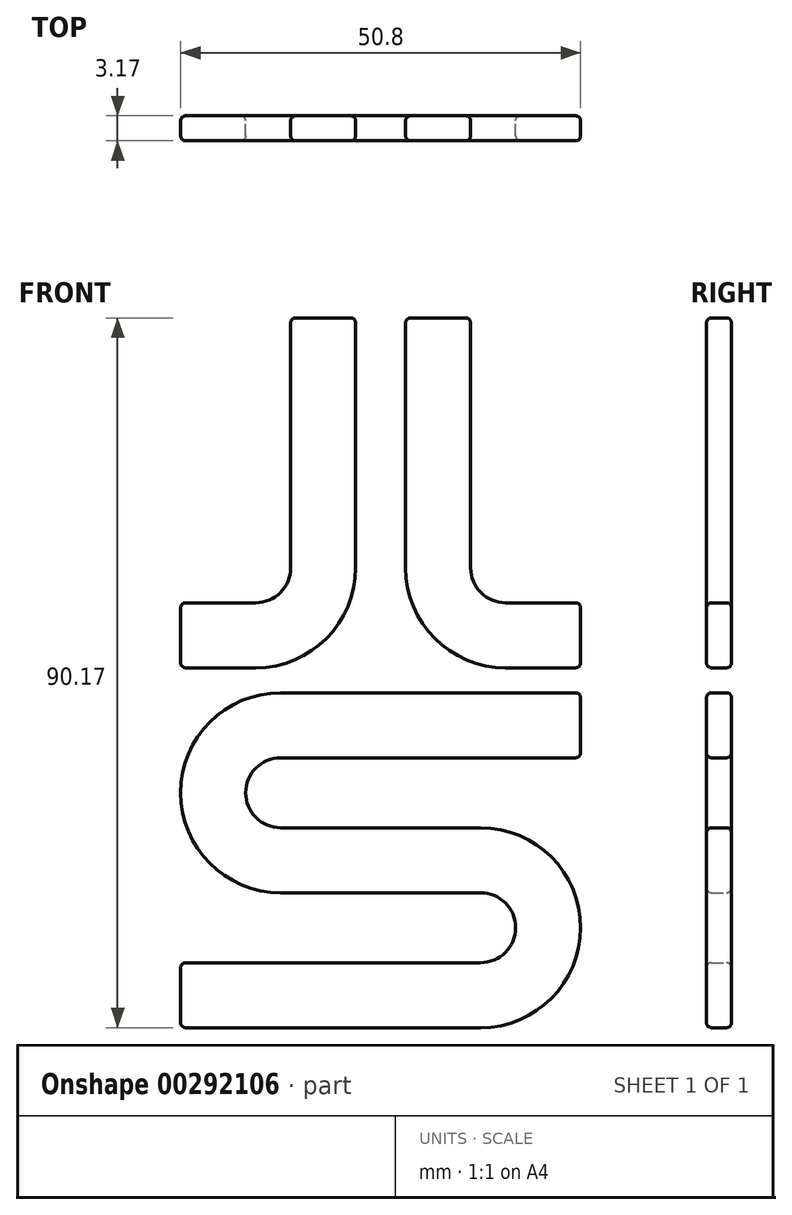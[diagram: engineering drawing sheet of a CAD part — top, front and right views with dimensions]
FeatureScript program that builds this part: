
annotation { "Feature Type Name" : "Feature", "Feature Type Description" : "" }
export const myFeature = defineFeature(function(context is Context, id is Id, definition is map)
    precondition{}
    {
        {
            var Q0;
            Q0=qCreatedBy(makeId("Front.planeOp"),FACE);
            var sketch = newSketch(context, id + "F0", { "sketchPlane" : qUnion([Q0])});
            skLineSegment(sketch, "E0.bottom", {"start": v(-11.43, 44.45) * mm, "end": v(-3.17, 44.45) * mm});
            skLineSegment(sketch, "E0.left", {"start": v(-11.43, 44.45) * mm, "end": v(-11.43, 12.7) * mm});
            skLineSegment(sketch, "E0.right", {"start": v(-3.17, 44.45) * mm, "end": v(-3.17, 12.7) * mm});
            skLineSegment(sketch, "E1.bottom", {"start": v(-15.87, 8.26) * mm, "end": v(-25.4, 8.26) * mm});
            skLineSegment(sketch, "E1.top", {"start": v(-15.87, 0) * mm, "end": v(-25.4, 0) * mm});
            skLineSegment(sketch, "E1.right", {"start": v(-25.4, 8.26) * mm, "end": v(-25.4, 0) * mm});
            skArc(sketch, "E2", {"start": v(-11.43, 12.7) * mm, "mid": v(-12.73, 9.56) * mm, "end": v(-15.87, 8.26) * mm});
            skArc(sketch, "E3", {"start": v(-3.17, 12.7) * mm, "mid": v(-6.9, 3.72) * mm, "end": v(-15.87, 0) * mm});
            skLineSegment(sketch, "E4", {"start": v(0, 0) * mm, "end": v(0, 65.18) * mm, "construction": true});
            skLineSegment(sketch, "E5.MirrorCS", {"start": v(11.43, 44.45) * mm, "end": v(3.17, 44.45) * mm});
            skLineSegment(sketch, "E6.MirrorCS", {"start": v(11.43, 44.45) * mm, "end": v(11.43, 12.7) * mm});
            skLineSegment(sketch, "E7.MirrorCS", {"start": v(3.17, 44.45) * mm, "end": v(3.17, 12.7) * mm});
            skArc(sketch, "E8.MirrorCS", {"start": v(3.17, 12.7) * mm, "mid": v(6.9, 3.72) * mm, "end": v(15.87, 0) * mm});
            skArc(sketch, "E9.MirrorCS", {"start": v(11.43, 12.7) * mm, "mid": v(12.73, 9.56) * mm, "end": v(15.87, 8.26) * mm});
            skLineSegment(sketch, "E10.MirrorCS", {"start": v(15.87, 8.26) * mm, "end": v(25.4, 8.26) * mm});
            skLineSegment(sketch, "E11.MirrorCS", {"start": v(15.87, 0) * mm, "end": v(25.4, 0) * mm});
            skLineSegment(sketch, "E12.MirrorCS", {"start": v(25.4, 8.26) * mm, "end": v(25.4, 0) * mm});
            skLineSegment(sketch, "E13.bottom", {"start": v(25.4, -3.17) * mm, "end": v(-12.7, -3.17) * mm});
            skLineSegment(sketch, "E13.top", {"start": v(25.4, -11.43) * mm, "end": v(-12.7, -11.43) * mm});
            skLineSegment(sketch, "E13.left", {"start": v(25.4, -3.17) * mm, "end": v(25.4, -11.43) * mm});
            skLineSegment(sketch, "E14.bottom", {"start": v(12.7, -20.32) * mm, "end": v(-12.7, -20.32) * mm});
            skLineSegment(sketch, "E14.top", {"start": v(12.7, -28.57) * mm, "end": v(-12.7, -28.57) * mm});
            skLineSegment(sketch, "E15.bottom", {"start": v(12.7, -37.46) * mm, "end": v(-25.4, -37.46) * mm});
            skLineSegment(sketch, "E15.top", {"start": v(12.7, -45.72) * mm, "end": v(-25.4, -45.72) * mm});
            skLineSegment(sketch, "E15.right", {"start": v(-25.4, -37.46) * mm, "end": v(-25.4, -45.72) * mm});
            skArc(sketch, "E16", {"start": v(-12.7, -11.43) * mm, "mid": v(-17.15, -15.87) * mm, "end": v(-12.7, -20.32) * mm});
            skArc(sketch, "E17", {"start": v(-12.7, -3.17) * mm, "mid": v(-25.4, -15.87) * mm, "end": v(-12.7, -28.57) * mm});
            skArc(sketch, "E18", {"start": v(12.7, -20.32) * mm, "mid": v(25.4, -33.02) * mm, "end": v(12.7, -45.72) * mm});
            skArc(sketch, "E19", {"start": v(12.7, -28.57) * mm, "mid": v(17.15, -33.02) * mm, "end": v(12.7, -37.46) * mm});
            skLineSegment(sketch, "E20", {"start": v(25.4, -11.43) * mm, "end": v(25.4, -33.02) * mm, "construction": true});
            skLineSegment(sketch, "E21", {"start": v(-25.4, -37.46) * mm, "end": v(-25.4, -15.87) * mm, "construction": true});
            skLineSegment(sketch, "E22", {"start": v(25.4, 0) * mm, "end": v(25.4, -3.17) * mm, "construction": true});
            skLineSegment(sketch, "E23", {"start": v(-12.7, -3.17) * mm, "end": v(-12.7, -11.43) * mm, "construction": true});
            skLineSegment(sketch, "E24", {"start": v(12.7, -20.32) * mm, "end": v(12.7, -28.57) * mm, "construction": true});
            skLineSegment(sketch, "E25", {"start": v(12.7, -37.46) * mm, "end": v(12.7, -45.72) * mm, "construction": true});
            skLineSegment(sketch, "E26", {"start": v(-3.17, 44.45) * mm, "end": v(0, 44.45) * mm, "construction": true});
            skSolve(sketch);
        }
        {
            var Q0;
            Q0 = qSketchRegion(id + "F0", true);
            extrude(context, id + "F1", {"entities" : qUnion([Q0]), "depth" : 3.17 * mm});
        }
        {
            var Q0;
            Q0=makeQuery(id+"F1.opExtrude","CAP_FACE",FACE,{"disambiguationData":[OSD([sQuery(id+"F0.wireOp",EDGE,"E13.bottom"),sQuery(id+"F0.wireOp",EDGE,"E13.top"),sQuery(id+"F0.wireOp",EDGE,"E13.left"),sQuery(id+"F0.wireOp",EDGE,"E14.bottom"),sQuery(id+"F0.wireOp",EDGE,"E14.top"),sQuery(id+"F0.wireOp",EDGE,"E15.bottom"),sQuery(id+"F0.wireOp",EDGE,"E15.top"),sQuery(id+"F0.wireOp",EDGE,"E15.right"),sQuery(id+"F0.wireOp",EDGE,"E16"),sQuery(id+"F0.wireOp",EDGE,"E17"),sQuery(id+"F0.wireOp",EDGE,"E18"),sQuery(id+"F0.wireOp",EDGE,"E19")])],"isStart":false});
            var sketch = newSketch(context, id + "F2", { "sketchPlane" : qUnion([Q0])});
            skSolve(sketch);
        }
        {
            var Q0;
            Q0=makeQuery(id+"F1.opExtrude","CAP_FACE",FACE,{"disambiguationData":[OSD([sQuery(id+"F0.wireOp",EDGE,"E5.MirrorCS"),sQuery(id+"F0.wireOp",EDGE,"E6.MirrorCS"),sQuery(id+"F0.wireOp",EDGE,"E7.MirrorCS"),sQuery(id+"F0.wireOp",EDGE,"E8.MirrorCS"),sQuery(id+"F0.wireOp",EDGE,"E9.MirrorCS"),sQuery(id+"F0.wireOp",EDGE,"E10.MirrorCS"),sQuery(id+"F0.wireOp",EDGE,"E11.MirrorCS"),sQuery(id+"F0.wireOp",EDGE,"E12.MirrorCS")])],"isStart":false});
            var Q1;
            Q1=makeQuery(id+"F1.opExtrude","CAP_FACE",FACE,{"disambiguationData":[OSD([sQuery(id+"F0.wireOp",EDGE,"E0.bottom"),sQuery(id+"F0.wireOp",EDGE,"E0.left"),sQuery(id+"F0.wireOp",EDGE,"E0.right"),sQuery(id+"F0.wireOp",EDGE,"E1.bottom"),sQuery(id+"F0.wireOp",EDGE,"E1.top"),sQuery(id+"F0.wireOp",EDGE,"E1.right"),sQuery(id+"F0.wireOp",EDGE,"E2"),sQuery(id+"F0.wireOp",EDGE,"E3")])],"isStart":false});
            var Q2;
            Q2=makeQuery(id+"F1.opExtrude","CAP_FACE",FACE,{"disambiguationData":[OSD([sQuery(id+"F0.wireOp",EDGE,"E13.bottom"),sQuery(id+"F0.wireOp",EDGE,"E13.top"),sQuery(id+"F0.wireOp",EDGE,"E13.left"),sQuery(id+"F0.wireOp",EDGE,"E14.bottom"),sQuery(id+"F0.wireOp",EDGE,"E14.top"),sQuery(id+"F0.wireOp",EDGE,"E15.bottom"),sQuery(id+"F0.wireOp",EDGE,"E15.top"),sQuery(id+"F0.wireOp",EDGE,"E15.right"),sQuery(id+"F0.wireOp",EDGE,"E16"),sQuery(id+"F0.wireOp",EDGE,"E17"),sQuery(id+"F0.wireOp",EDGE,"E18"),sQuery(id+"F0.wireOp",EDGE,"E19")])],"isStart":false});
            var Q3;
            Q3=makeQuery(id+"F1.opExtrude","SWEPT_FACE",FACE,{"disambiguationData":[OSD([sQuery(id+"F0.wireOp",EDGE,"E12.MirrorCS")])]});
            var Q4;
            Q4=makeQuery(id+"F1.opExtrude","SWEPT_FACE",FACE,{"disambiguationData":[OSD([sQuery(id+"F0.wireOp",EDGE,"E13.left")])]});
            var Q5;
            Q5=makeQuery(id+"F1.opExtrude","SWEPT_FACE",FACE,{"disambiguationData":[OSD([sQuery(id+"F0.wireOp",EDGE,"E18")])]});
            var Q6;
            Q6=makeQuery(id+"F1.opExtrude","SWEPT_FACE",FACE,{"disambiguationData":[OSD([sQuery(id+"F0.wireOp",EDGE,"E15.bottom")])]});
            var Q7;
            Q7=makeQuery(id+"F1.opExtrude","SWEPT_FACE",FACE,{"disambiguationData":[OSD([sQuery(id+"F0.wireOp",EDGE,"E1.right")])]});
            var Q8;
            Q8=makeQuery(id+"F1.opExtrude","SWEPT_FACE",FACE,{"disambiguationData":[OSD([sQuery(id+"F0.wireOp",EDGE,"E5.MirrorCS")])]});
            var Q9;
            Q9=makeQuery(id+"F1.opExtrude","SWEPT_FACE",FACE,{"disambiguationData":[OSD([sQuery(id+"F0.wireOp",EDGE,"E0.bottom")])]});
            var Q10;
            Q10=makeQuery(id+"F1.opExtrude","CAP_FACE",FACE,{"disambiguationData":[OSD([sQuery(id+"F0.wireOp",EDGE,"E0.bottom"),sQuery(id+"F0.wireOp",EDGE,"E0.left"),sQuery(id+"F0.wireOp",EDGE,"E0.right"),sQuery(id+"F0.wireOp",EDGE,"E1.bottom"),sQuery(id+"F0.wireOp",EDGE,"E1.top"),sQuery(id+"F0.wireOp",EDGE,"E1.right"),sQuery(id+"F0.wireOp",EDGE,"E2"),sQuery(id+"F0.wireOp",EDGE,"E3")])],"isStart":true});
            var Q11;
            Q11=makeQuery(id+"F1.opExtrude","CAP_FACE",FACE,{"disambiguationData":[OSD([sQuery(id+"F0.wireOp",EDGE,"E5.MirrorCS"),sQuery(id+"F0.wireOp",EDGE,"E6.MirrorCS"),sQuery(id+"F0.wireOp",EDGE,"E7.MirrorCS"),sQuery(id+"F0.wireOp",EDGE,"E8.MirrorCS"),sQuery(id+"F0.wireOp",EDGE,"E9.MirrorCS"),sQuery(id+"F0.wireOp",EDGE,"E10.MirrorCS"),sQuery(id+"F0.wireOp",EDGE,"E11.MirrorCS"),sQuery(id+"F0.wireOp",EDGE,"E12.MirrorCS")])],"isStart":true});
            var Q12;
            Q12=makeQuery(id+"F1.opExtrude","CAP_FACE",FACE,{"disambiguationData":[OSD([sQuery(id+"F0.wireOp",EDGE,"E13.bottom"),sQuery(id+"F0.wireOp",EDGE,"E13.top"),sQuery(id+"F0.wireOp",EDGE,"E13.left"),sQuery(id+"F0.wireOp",EDGE,"E14.bottom"),sQuery(id+"F0.wireOp",EDGE,"E14.top"),sQuery(id+"F0.wireOp",EDGE,"E15.bottom"),sQuery(id+"F0.wireOp",EDGE,"E15.top"),sQuery(id+"F0.wireOp",EDGE,"E15.right"),sQuery(id+"F0.wireOp",EDGE,"E16"),sQuery(id+"F0.wireOp",EDGE,"E17"),sQuery(id+"F0.wireOp",EDGE,"E18"),sQuery(id+"F0.wireOp",EDGE,"E19")])],"isStart":true});
            var Q13;
            Q13=makeQuery(id+"F1.opExtrude","SWEPT_EDGE",EDGE,{"disambiguationData":[OSD([sQuery(id+"F0.wireOp",EDGE,"E15.top"),sQuery(id+"F0.wireOp",EDGE,"E15.right")])]});
            fillet(context, id + "F3", {"entities" : qUnion([Q0, Q1, Q2, Q3, Q4, Q5, Q6, Q7, Q8, Q9, Q10, Q11, Q12, Q13]), "radius" : 0.64 * mm, "tangentPropagation" : true, "allowEdgeOverflow" : false});
        }
    });
